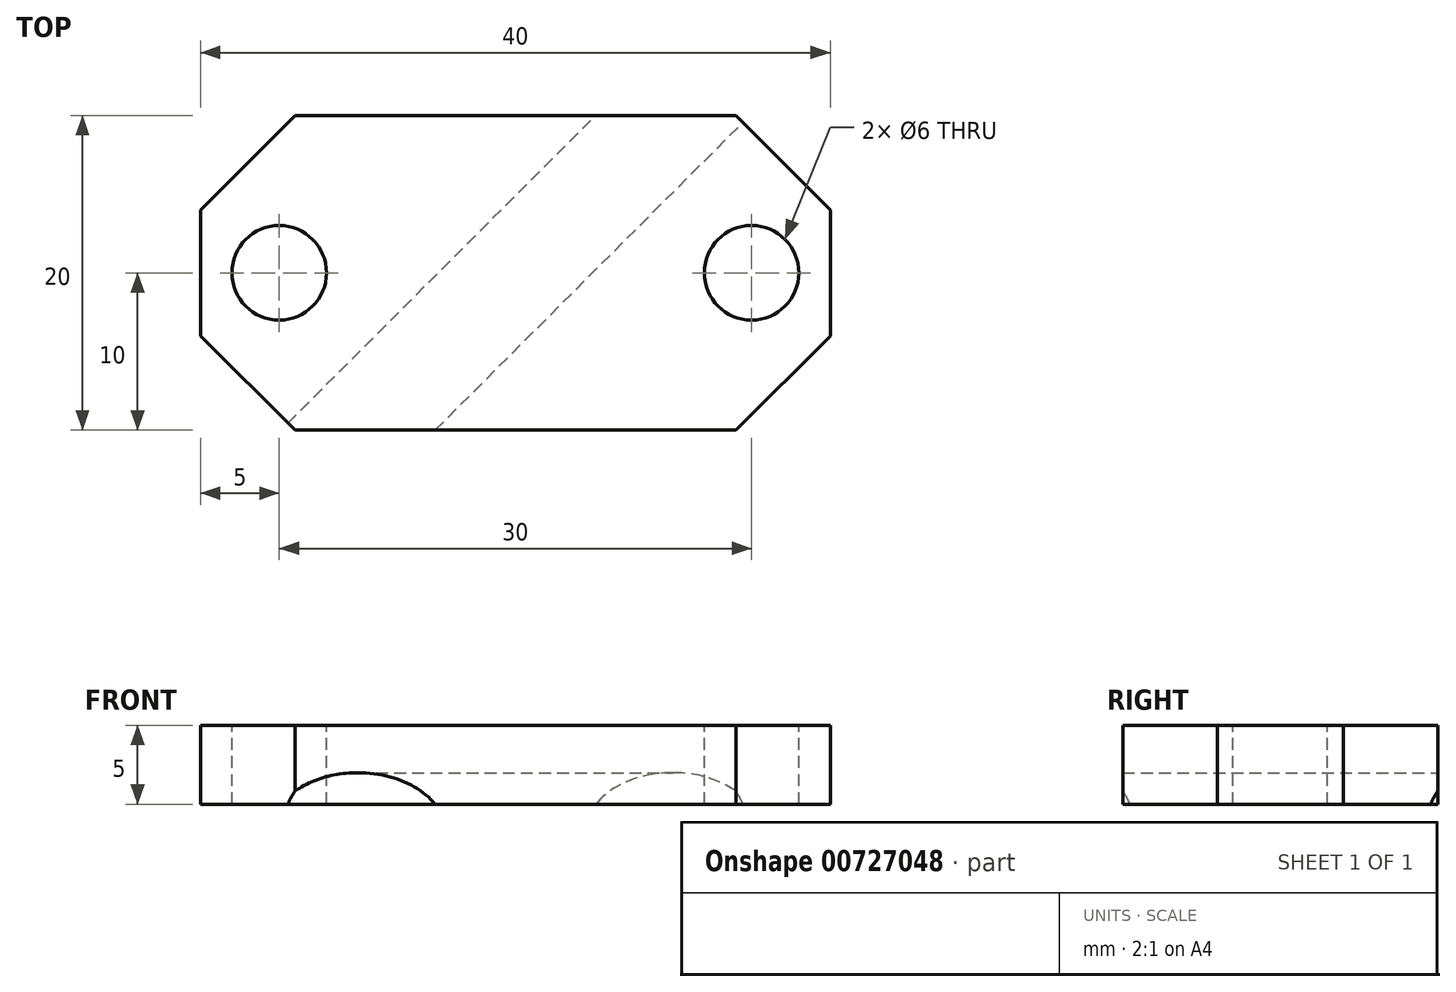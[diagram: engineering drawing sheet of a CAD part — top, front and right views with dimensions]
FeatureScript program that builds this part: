
annotation { "Feature Type Name" : "Feature", "Feature Type Description" : "" }
export const myFeature = defineFeature(function(context is Context, id is Id, definition is map)
    precondition{}
    {
        {
            var Q0;
            Q0=qCreatedBy(makeId("Front.planeOp"),FACE);
            var sketch = newSketch(context, id + "F0", { "sketchPlane" : qUnion([Q0])});
            skCircle(sketch, "E0", {"center": v(0, 0) * mm, "radius": 4 * mm});
            skLineSegment(sketch, "E1.bottom", {"start": v(20, 2) * mm, "end": v(-20, 2) * mm});
            skLineSegment(sketch, "E1.top", {"start": v(20, 7) * mm, "end": v(-20, 7) * mm});
            skLineSegment(sketch, "E1.left", {"start": v(20, 2) * mm, "end": v(20, 7) * mm});
            skLineSegment(sketch, "E1.right", {"start": v(-20, 2) * mm, "end": v(-20, 7) * mm});
            skSolve(sketch);
        }
        {
            var Q0;
            Q0=makeQuery(id+"F0.imprint","IMPRINT",FACE,{"disambiguationData":[TD([[makeQuery(id+"F0.imprint","IMPRINT",EDGE,{"derivedFrom":sQuery(id+"F0.wireOp",EDGE,"E1.top")}),1.0]])]});
            var Q1;
            {var subQ0=sQuery(id+"F0.wireOp",EDGE,"E1.bottom");var subQ1=sQuery(id+"F0.wireOp",EDGE,"E0");var subQ2=makeQuery(id+"F0.imprint","INTERSECT",VERTEX,{"disambiguationData":[OD(0.0)],"derivedFrom":[subQ1,subQ0]});Q1=makeQuery(id+"F0.imprint","IMPRINT",FACE,{"disambiguationData":[TD([[makeQuery(id+"F0.imprint","IMPRINT",EDGE,{"disambiguationData":[TD([[subQ2,-1.0]])],"derivedFrom":subQ1}),1.0]])]});}
            extrude(context, id + "F1", {"entities" : qUnion([Q0, Q1]), "endBound" : BoundingType.SYMMETRIC, "depth" : 20 * mm, "offsetDistance" : 25 * mm});
        }
        {
            var Q0;
            Q0=makeQuery(id+"F1.opExtrude","SWEPT_FACE",FACE,{"disambiguationData":[OSD([sQuery(id+"F0.wireOp",EDGE,"E1.top")])]});
            var sketch = newSketch(context, id + "F2", { "sketchPlane" : qUnion([Q0])});
            skPoint(sketch, "E2", {"position": v(-15, 0) * mm});
            skPoint(sketch, "E3", {"position": v(15, 0) * mm});
            skSolve(sketch);
        }
        {
            var Q0;
            Q0=sQuery(id+"F2.wireOp",VERTEX,"E3");
            var Q1;
            Q1=sQuery(id+"F2.wireOp",VERTEX,"E2");
            var Q2;
            Q2=makeQuery(id+"F1.opExtrude","SWEPT_BODY",BODY,{"disambiguationData":[OSD([sQuery(id+"F0.wireOp",EDGE,"E0"),sQuery(id+"F0.wireOp",EDGE,"E1.bottom"),sQuery(id+"F0.wireOp",EDGE,"E1.top"),sQuery(id+"F0.wireOp",EDGE,"E1.left"),sQuery(id+"F0.wireOp",EDGE,"E1.right")])]});
            hole(context, id + "F3", {"style" : HoleStyle.SIMPLE, "endStyle" : HoleEndStyle.THROUGH, "holeDiameter" : 6 * mm, "majorDiameter" : 5 * mm, "isTappedThrough" : true, "tappedDepth" : 12 * mm, "tapClearance" : 3, "locations" : qUnion([Q0, Q1]), "scope" : qUnion([Q2])});
        }
        {
            var Q0;
            Q0=qCreatedBy(makeId("Right.planeOp"),FACE);
            var Q1;
            Q1=qCreatedBy(makeId("Front.planeOp"),FACE);
            cPlane(context, id + "F4", {"entities" : qUnion([Q0, Q1]), "cplaneType" : CPlaneType.MID_PLANE, "offset" : 25 * mm, "width" : 150 * mm, "height" : 150 * mm});
        }
        {
            var Q0;
            Q0=qCreatedBy(id+"F4.planeOp",FACE);
            var sketch = newSketch(context, id + "F5", { "sketchPlane" : qUnion([Q0])});
            skCircle(sketch, "E4", {"center": v(0, 0) * mm, "radius": 4 * mm});
            skSolve(sketch);
        }
        {
            var Q0;
            Q0=makeQuery(id+"F5.imprint","IMPRINT",FACE,{"disambiguationData":[TD([[makeQuery(id+"F5.imprint","IMPRINT",EDGE,{"derivedFrom":sQuery(id+"F5.wireOp",EDGE,"E4")}),1.0]])]});
            extrude(context, id + "F6", {"entities" : qUnion([Q0]), "operationType" : NewBodyOperationType.REMOVE, "endBound" : BoundingType.SYMMETRIC, "oppositeDirection" : true, "depth" : 60 * mm, "offsetDistance" : 25 * mm});
        }
        {
            var Q0;
            Q0=makeQuery(id+"F1.opExtrude","CAP_EDGE",EDGE,{"disambiguationData":[OSD([sQuery(id+"F0.wireOp",EDGE,"E1.right")])],"isStart":false});
            var Q1;
            Q1=makeQuery(id+"F1.opExtrude","CAP_EDGE",EDGE,{"disambiguationData":[OSD([sQuery(id+"F0.wireOp",EDGE,"E1.left")])],"isStart":true});
            var Q2;
            Q2=makeQuery(id+"F1.opExtrude","CAP_EDGE",EDGE,{"disambiguationData":[OSD([sQuery(id+"F0.wireOp",EDGE,"E1.left")])],"isStart":false});
            var Q3;
            Q3=makeQuery(id+"F1.opExtrude","CAP_EDGE",EDGE,{"disambiguationData":[OSD([sQuery(id+"F0.wireOp",EDGE,"E1.right")])],"isStart":true});
            chamfer(context, id + "F7", {"entities" : qUnion([Q0, Q1, Q2, Q3]), "width" : 6 * mm, "tangentPropagation" : true});
        }
    });
